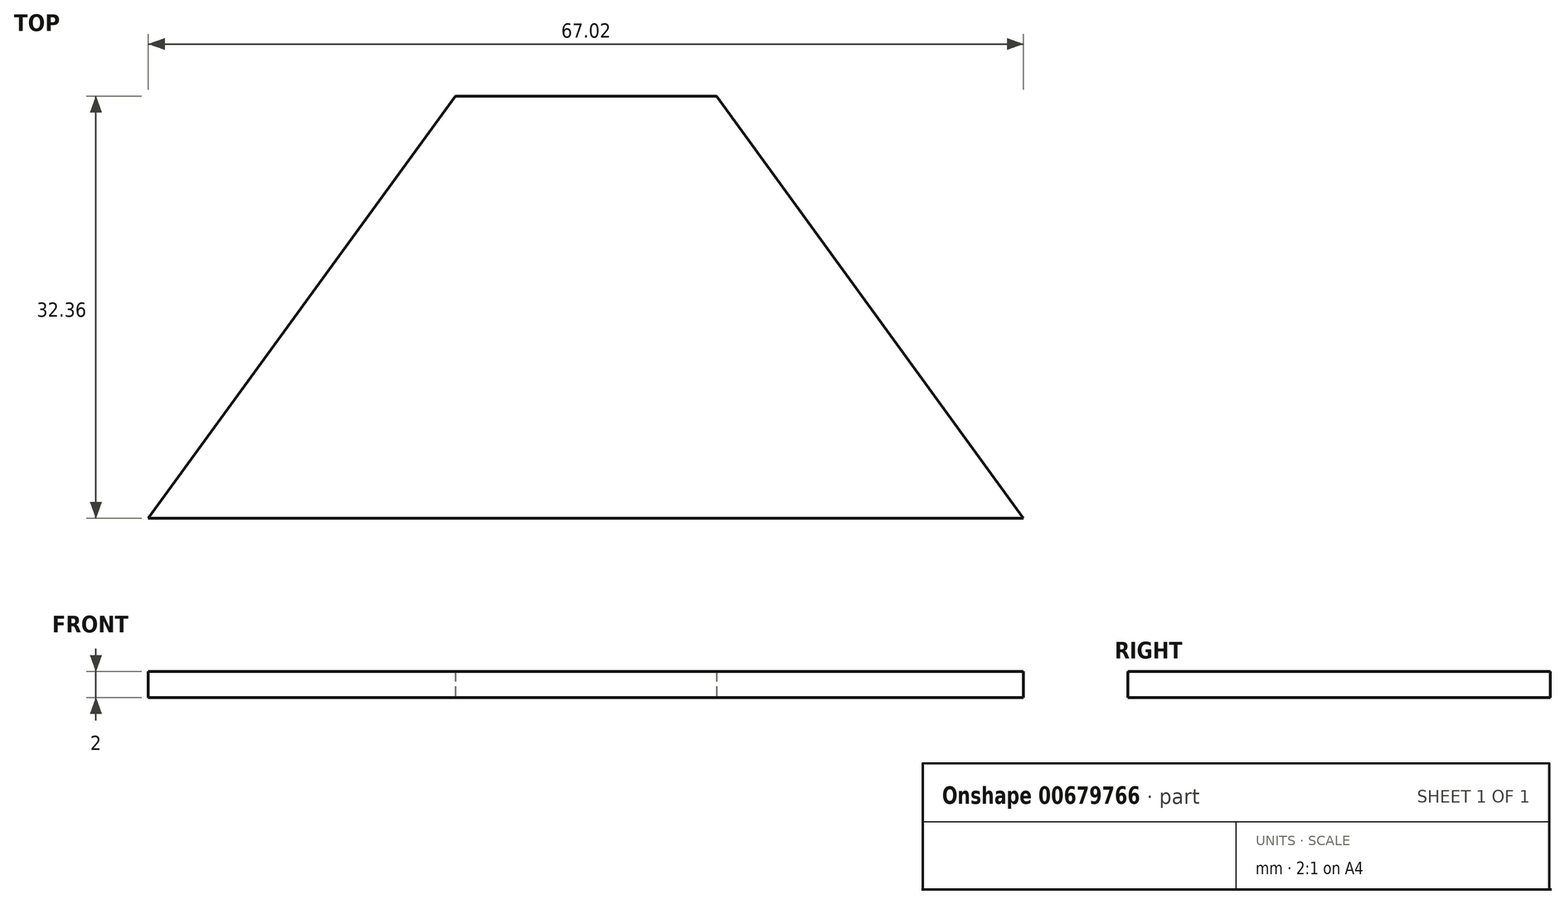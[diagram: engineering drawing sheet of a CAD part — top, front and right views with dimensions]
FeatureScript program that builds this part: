
annotation { "Feature Type Name" : "Feature", "Feature Type Description" : "" }
export const myFeature = defineFeature(function(context is Context, id is Id, definition is map)
    precondition{}
    {
        {
            var Q0;
            Q0=qCreatedBy(makeId("Top.planeOp"),FACE);
            var sketch = newSketch(context, id + "F0", { "sketchPlane" : qUnion([Q0])});
            skLineSegment(sketch, "E0", {"start": v(-8.1, -2.33) * mm, "end": v(11.9, -2.33) * mm});
            skLineSegment(sketch, "E1", {"start": v(-8.1, -2.33) * mm, "end": v(-31.6, -34.7) * mm});
            skLineSegment(sketch, "E2", {"start": v(11.9, -2.33) * mm, "end": v(35.42, -34.7) * mm});
            skLineSegment(sketch, "E3", {"start": v(-31.6, -34.7) * mm, "end": v(35.42, -34.7) * mm});
            skPoint(sketch, "E4.startSnap0", {"position": v(1.9, -2.33) * mm});
            skPoint(sketch, "E4.endSnap0", {"position": v(1.9, -2.33) * mm});
            skPoint(sketch, "E5.startSnap0", {"position": v(-7.04, 7.44) * mm});
            skSolve(sketch);
        }
        {
            var Q0;
            Q0=makeQuery(id+"F0.imprint","IMPRINT",FACE,{"disambiguationData":[TD([[makeQuery(id+"F0.imprint","IMPRINT",EDGE,{"derivedFrom":sQuery(id+"F0.wireOp",EDGE,"E0")}),-1.0]])]});
            extrude(context, id + "F1", {"entities" : qUnion([Q0]), "depth" : 2 * mm, "offsetDistance" : 25 * mm});
        }
    });
